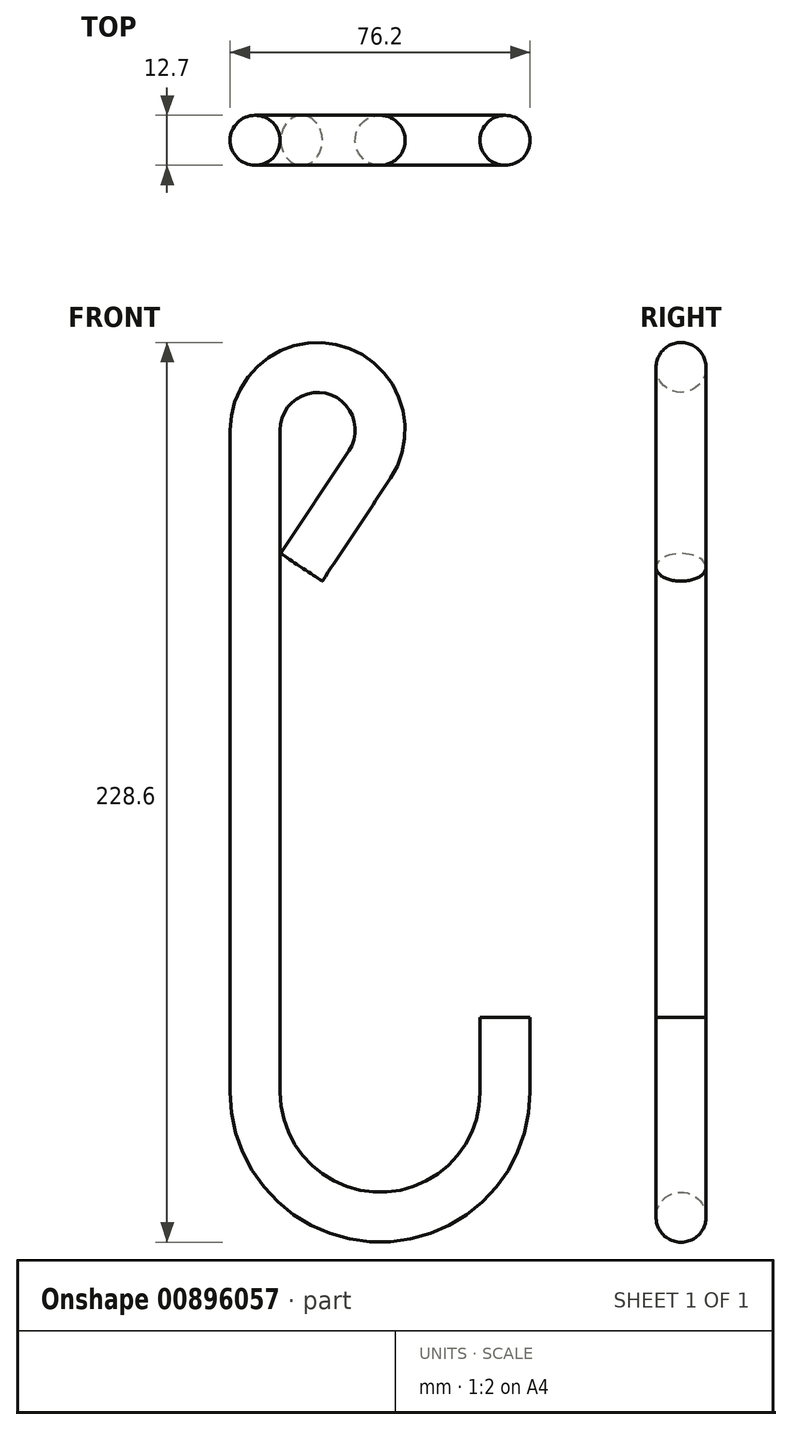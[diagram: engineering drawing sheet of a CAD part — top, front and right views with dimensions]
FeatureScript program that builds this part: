
annotation { "Feature Type Name" : "Feature", "Feature Type Description" : "" }
export const myFeature = defineFeature(function(context is Context, id is Id, definition is map)
    precondition{}
    {
        {
            var Q0;
            Q0=qCreatedBy(makeId("Front.planeOp"),FACE);
            var sketch = newSketch(context, id + "F0", { "sketchPlane" : qUnion([Q0])});
            skArc(sketch, "E0", {"start": v(-63.5, -19.05) * mm, "mid": v(-31.75, -50.8) * mm, "end": v(0, -19.05) * mm});
            skLineSegment(sketch, "E1", {"start": v(0, 0) * mm, "end": v(0, -19.05) * mm});
            skPoint(sketch, "E2", {"position": v(-31.75, -50.8) * mm});
            skPoint(sketch, "E3", {"position": v(-31.75, -57.15) * mm});
            skLineSegment(sketch, "E4", {"start": v(-63.5, -19.05) * mm, "end": v(-63.5, 149.22) * mm});
            skArc(sketch, "E5", {"start": v(-34.4, 140.45) * mm, "mid": v(-43.04, 164.42) * mm, "end": v(-63.5, 149.22) * mm});
            skPoint(sketch, "E6", {"position": v(-47.62, 171.45) * mm});
            skLineSegment(sketch, "E7", {"start": v(-34.4, 140.45) * mm, "end": v(-51.73, 114.3) * mm});
            skLineSegment(sketch, "E8", {"start": v(-57.02, 117.8) * mm, "end": v(-46.44, 110.8) * mm, "construction": true});
            skSolve(sketch);
        }
        {
            var Q0;
            Q0=qCreatedBy(makeId("Top.planeOp"),FACE);
            var sketch = newSketch(context, id + "F1", { "sketchPlane" : qUnion([Q0])});
            skCircle(sketch, "E9", {"center": v(0, 0) * mm, "radius": 6.35 * mm});
            skSolve(sketch);
        }
        {
            var Q0;
            Q0=makeQuery(id+"F1.imprint","IMPRINT",FACE,{"disambiguationData":[TD([[makeQuery(id+"F1.imprint","IMPRINT",EDGE,{"derivedFrom":sQuery(id+"F1.wireOp",EDGE,"E9")}),1.0]])]});
            var Q1;
            Q1 = qConstructionFilter(qBodyType(qCreatedBy(id + "F0" ,EDGE), BodyType.WIRE), ConstructionObject.NO);
            sweep(context, id + "F2", {"profiles" : qUnion([Q0]), "path" : qUnion([Q1])});
        }
    });
